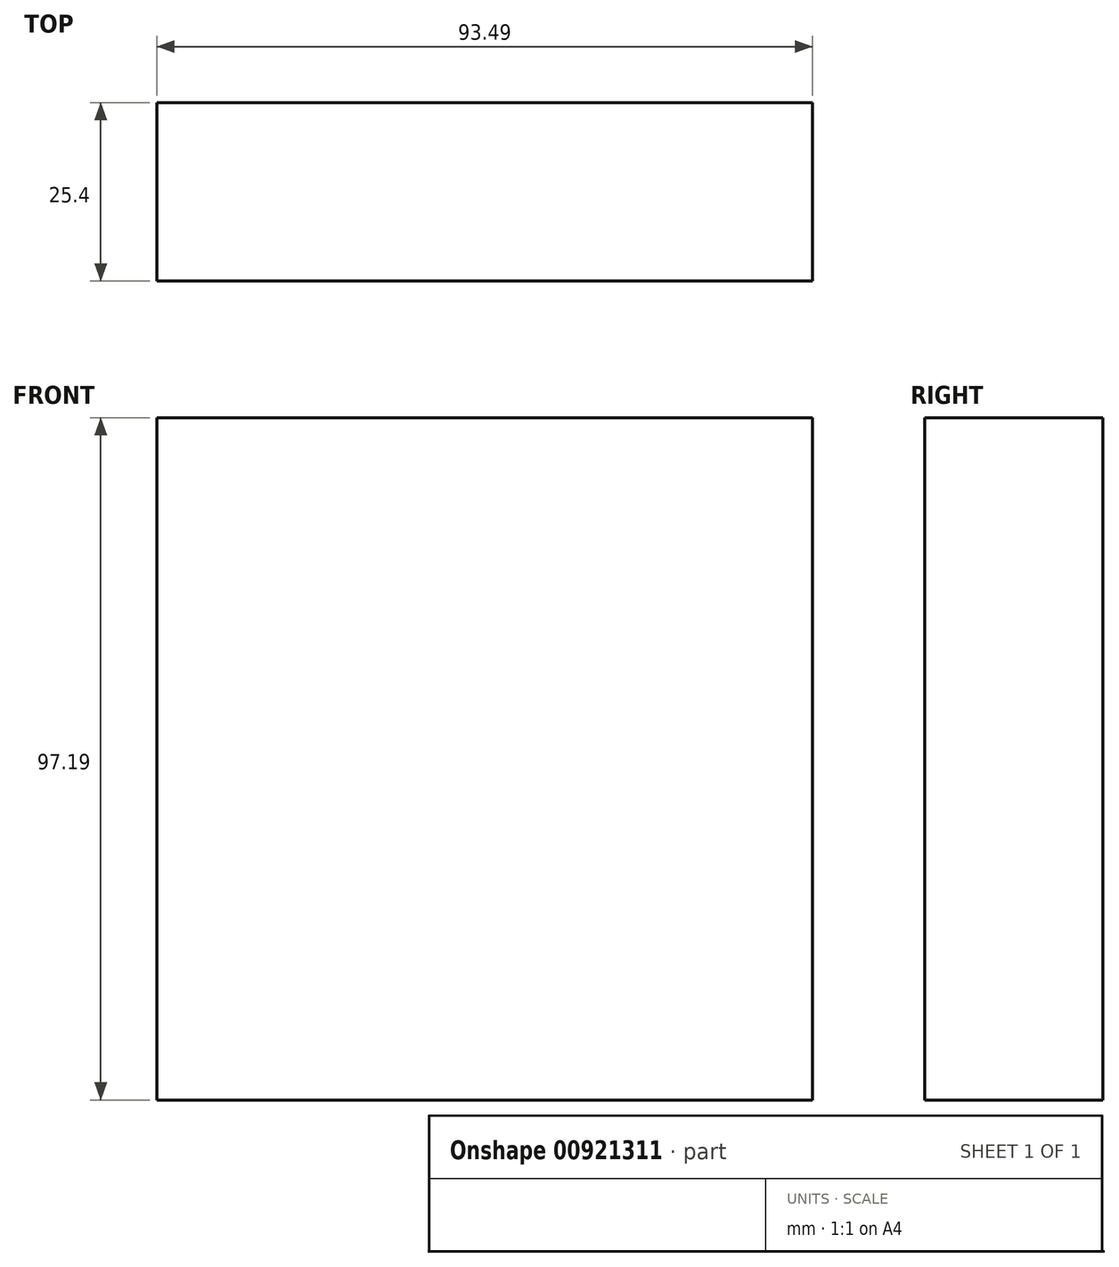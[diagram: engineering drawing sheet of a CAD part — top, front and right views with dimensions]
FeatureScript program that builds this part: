
annotation { "Feature Type Name" : "Feature", "Feature Type Description" : "" }
export const myFeature = defineFeature(function(context is Context, id is Id, definition is map)
    precondition{}
    {
        {
            var Q0;
            Q0=qCreatedBy(makeId("Front.planeOp"),FACE);
            var sketch = newSketch(context, id + "F0", { "sketchPlane" : qUnion([Q0])});
            skLineSegment(sketch, "E0.bottom", {"start": v(-46.2, 51.37) * mm, "end": v(47.3, 51.37) * mm});
            skLineSegment(sketch, "E0.top", {"start": v(-46.2, -45.82) * mm, "end": v(47.3, -45.82) * mm});
            skLineSegment(sketch, "E0.left", {"start": v(-46.2, 51.37) * mm, "end": v(-46.2, -45.82) * mm});
            skLineSegment(sketch, "E0.right", {"start": v(47.3, 51.37) * mm, "end": v(47.3, -45.82) * mm});
            skSolve(sketch);
        }
        {
            var Q0;
            Q0=makeQuery(id+"F0.imprint","IMPRINT",FACE,{"disambiguationData":[TD([[makeQuery(id+"F0.imprint","IMPRINT",EDGE,{"derivedFrom":sQuery(id+"F0.wireOp",EDGE,"E0.bottom")}),-1.0]])]});
            extrude(context, id + "F1", {"entities" : qUnion([Q0]), "depth" : 25.4 * mm, "offsetDistance" : 25.4 * mm});
        }
    });
